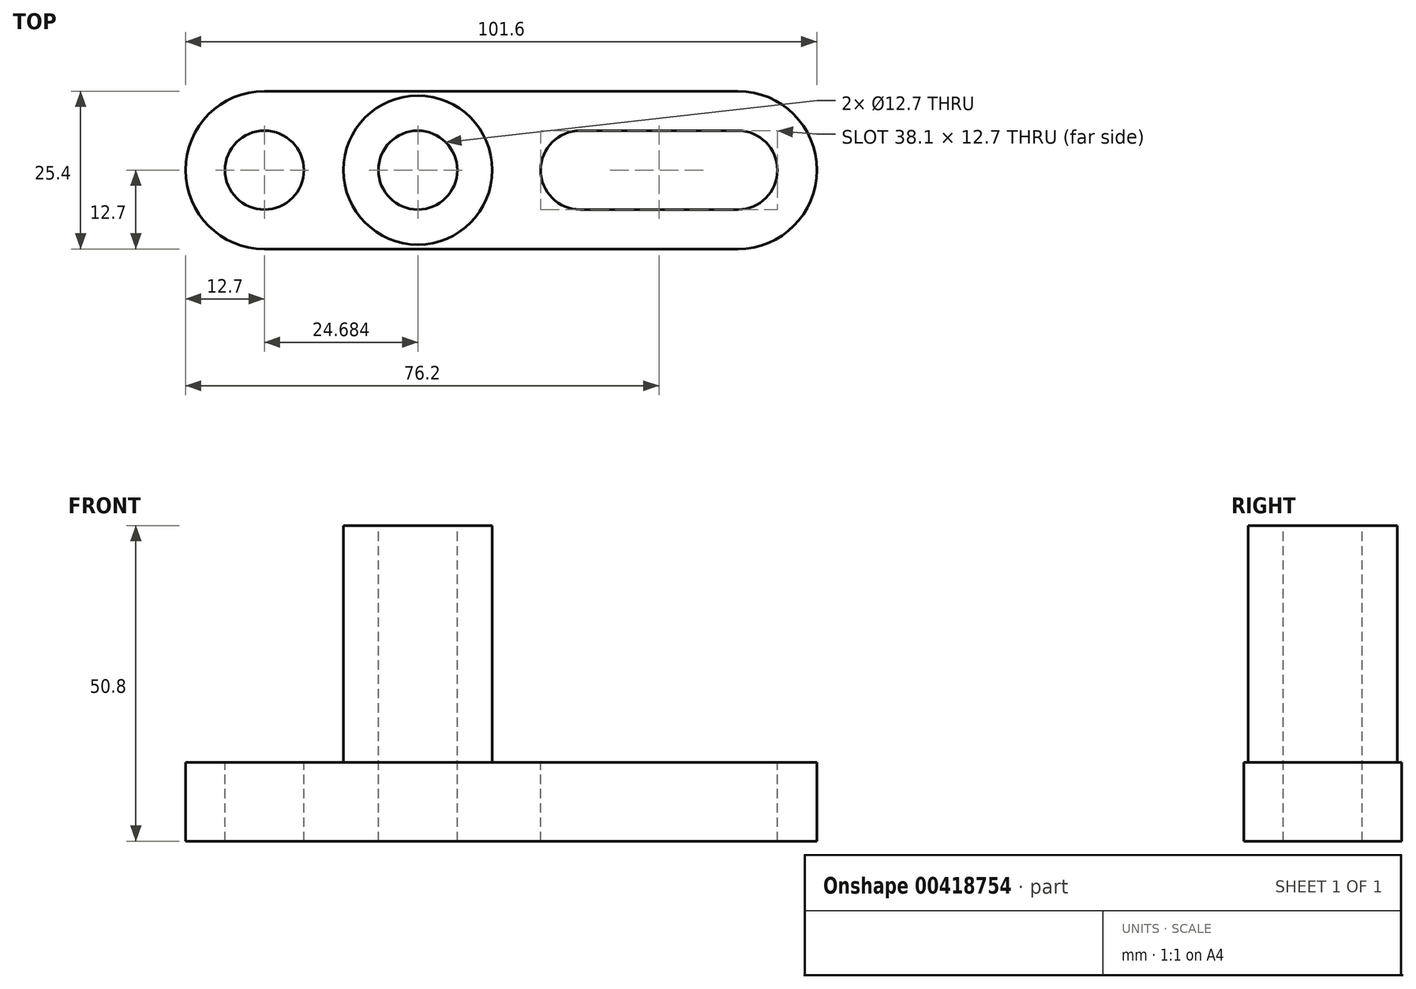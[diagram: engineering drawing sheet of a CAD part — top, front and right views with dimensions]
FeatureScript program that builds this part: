
annotation { "Feature Type Name" : "Feature", "Feature Type Description" : "" }
export const myFeature = defineFeature(function(context is Context, id is Id, definition is map)
    precondition{}
    {
        {
            var Q0;
            Q0=qCreatedBy(makeId("Front.planeOp"),FACE);
            var sketch = newSketch(context, id + "F0", { "sketchPlane" : qUnion([Q0])});
            skLineSegment(sketch, "E0", {"start": v(0, 0) * mm, "end": v(101.6, 0) * mm});
            skLineSegment(sketch, "E1", {"start": v(101.6, 0) * mm, "end": v(101.6, 12.7) * mm});
            skLineSegment(sketch, "E2", {"start": v(101.6, 12.7) * mm, "end": v(0, 12.7) * mm});
            skLineSegment(sketch, "E3", {"start": v(0, 12.7) * mm, "end": v(0, 0) * mm});
            skSolve(sketch);
        }
        {
            var Q0;
            Q0 = qSketchRegion(id + "F0", true);
            extrude(context, id + "F1", {"entities" : qUnion([Q0]), "depth" : 25.4 * mm});
        }
        {
            var Q0;
            {var subQ0=sQuery(id+"F0.wireOp",EDGE,"E2");var subQ1=makeQuery(id+"F1.opExtrude","SWEPT_FACE",FACE,{"disambiguationData":[OSD([subQ0])]});var subQ2=sQuery(id+"F0.wireOp",EDGE,"E1");Q0=makeQuery(id+"FwOSXB9rs8ltbqY_1.boolean.opBoolean","SPLIT",FACE,{"disambiguationData":[TD([makeQuery(id+"F1.opExtrude","SWEPT_FACE",FACE,{"disambiguationData":[OSD([subQ2])]})])],"derivedFrom":subQ1});}
            var sketch = newSketch(context, id + "F2", { "sketchPlane" : qUnion([Q0])});
            skArc(sketch, "E4", {"start": v(88.9, -25.4) * mm, "mid": v(101.6, -12.7) * mm, "end": v(88.9, 0) * mm});
            skArc(sketch, "E5", {"start": v(12.7, 0) * mm, "mid": v(0, -13.14) * mm, "end": v(12.67, -26.32) * mm});
            skSolve(sketch);
        }
        {
            var Q0;
            {var subQ0=sQuery(id+"F2.wireOp",EDGE,"E4");var subQ1=sQuery(id+"F0.wireOp",EDGE,"E2");var subQ2=sQuery(id+"F0.wireOp",EDGE,"E1");var subQ5=makeQuery(id+"F1.opExtrude","SWEPT_EDGE",EDGE,{"disambiguationData":[OSD([subQ2,subQ1])]});var subQ6=makeQuery(id+"F2.imprint","INTERSECT",VERTEX,{"derivedFrom":[subQ5,subQ0]});Q0=makeQuery(id+"F2.imprint","IMPRINT",FACE,{"disambiguationData":[TD([[makeQuery(id+"F2.imprint","IMPRINT",EDGE,{"disambiguationData":[TD([[subQ6,-1.0]])],"derivedFrom":subQ0}),-1.0]])]});}
            var Q1;
            {var subQ0=sQuery(id+"F2.wireOp",EDGE,"E4");var subQ1=sQuery(id+"F0.wireOp",EDGE,"E2");var subQ2=sQuery(id+"F0.wireOp",EDGE,"E1");var subQ5=makeQuery(id+"F1.opExtrude","SWEPT_EDGE",EDGE,{"disambiguationData":[OSD([subQ2,subQ1])]});var subQ6=makeQuery(id+"F2.imprint","INTERSECT",VERTEX,{"derivedFrom":[subQ5,subQ0]});Q1=makeQuery(id+"F2.imprint","IMPRINT",FACE,{"disambiguationData":[TD([[makeQuery(id+"F2.imprint","IMPRINT",EDGE,{"disambiguationData":[TD([[subQ6,1.0]])],"derivedFrom":subQ0}),-1.0]])]});}
            extrude(context, id + "F3", {"entities" : qUnion([Q0, Q1]), "operationType" : NewBodyOperationType.REMOVE, "oppositeDirection" : true, "depth" : 25.4 * mm});
        }
        {
            var Q0;
            {var subQ0=sQuery(id+"F0.wireOp",EDGE,"E3");var subQ1=sQuery(id+"F0.wireOp",EDGE,"E2");var subQ2=makeQuery(id+"F1.opExtrude","SWEPT_FACE",FACE,{"disambiguationData":[OSD([subQ1])]});Q0=makeQuery(id+"FwOSXB9rs8ltbqY_1.boolean.opBoolean","SPLIT",FACE,{"disambiguationData":[TD([makeQuery(id+"F1.opExtrude","SWEPT_FACE",FACE,{"disambiguationData":[OSD([subQ0])]})])],"derivedFrom":subQ2});}
            var sketch = newSketch(context, id + "F4", { "sketchPlane" : qUnion([Q0])});
            skArc(sketch, "E6", {"start": v(12.7, 0) * mm, "mid": v(0, -12.7) * mm, "end": v(12.7, -25.4) * mm});
            skSolve(sketch);
        }
        {
            var Q0;
            {var subQ0=sQuery(id+"F4.wireOp",EDGE,"E6");var subQ1=sQuery(id+"F0.wireOp",EDGE,"E3");var subQ2=sQuery(id+"F0.wireOp",EDGE,"E2");var subQ5=makeQuery(id+"F1.opExtrude","SWEPT_EDGE",EDGE,{"disambiguationData":[OSD([subQ2,subQ1])]});var subQ6=makeQuery(id+"F4.imprint","INTERSECT",VERTEX,{"derivedFrom":[subQ5,subQ0]});Q0=makeQuery(id+"F4.imprint","IMPRINT",FACE,{"disambiguationData":[TD([[makeQuery(id+"F4.imprint","IMPRINT",EDGE,{"disambiguationData":[TD([[subQ6,1.0]])],"derivedFrom":subQ0}),-1.0]])]});}
            var Q1;
            {var subQ0=sQuery(id+"F4.wireOp",EDGE,"E6");var subQ1=sQuery(id+"F0.wireOp",EDGE,"E3");var subQ2=sQuery(id+"F0.wireOp",EDGE,"E2");var subQ5=makeQuery(id+"F1.opExtrude","SWEPT_EDGE",EDGE,{"disambiguationData":[OSD([subQ2,subQ1])]});var subQ6=makeQuery(id+"F4.imprint","INTERSECT",VERTEX,{"derivedFrom":[subQ5,subQ0]});Q1=makeQuery(id+"F4.imprint","IMPRINT",FACE,{"disambiguationData":[TD([[makeQuery(id+"F4.imprint","IMPRINT",EDGE,{"disambiguationData":[TD([[subQ6,-1.0]])],"derivedFrom":subQ0}),-1.0]])]});}
            extrude(context, id + "F5", {"entities" : qUnion([Q0, Q1]), "operationType" : NewBodyOperationType.REMOVE, "oppositeDirection" : true, "depth" : 25.4 * mm});
        }
        {
            var Q0;
            Q0=makeQuery(id+"F1.opExtrude","SWEPT_FACE",FACE,{"disambiguationData":[OSD([sQuery(id+"F0.wireOp",EDGE,"E2")])]});
            var sketch = newSketch(context, id + "F6", { "sketchPlane" : qUnion([Q0])});
            skCircle(sketch, "E7", {"center": v(12.7, -12.7) * mm, "radius": 6.35 * mm});
            skSolve(sketch);
        }
        {
            var Q0;
            Q0 = qSketchRegion(id + "F6", true);
            extrude(context, id + "F7", {"entities" : qUnion([Q0]), "operationType" : NewBodyOperationType.REMOVE, "oppositeDirection" : true, "depth" : 25.4 * mm});
        }
        {
            var Q0;
            Q0=makeQuery(id+"F1.opExtrude","SWEPT_FACE",FACE,{"disambiguationData":[OSD([sQuery(id+"F0.wireOp",EDGE,"E2")])]});
            var sketch = newSketch(context, id + "F8", { "sketchPlane" : qUnion([Q0])});
            skCircle(sketch, "E8", {"center": v(37.38, -12.7) * mm, "radius": 11.98 * mm});
            skSolve(sketch);
        }
        {
            var Q0;
            Q0=makeQuery(id+"F8.imprint","IMPRINT",FACE,{"disambiguationData":[TD([[makeQuery(id+"F8.imprint","IMPRINT",EDGE,{"derivedFrom":sQuery(id+"F8.wireOp",EDGE,"E8")}),1.0]])]});
            extrude(context, id + "F9", {"entities" : qUnion([Q0]), "operationType" : NewBodyOperationType.ADD, "depth" : 38.1 * mm});
        }
        {
            var Q0;
            Q0=makeQuery(id+"F9.opExtrude","CAP_FACE",FACE,{"disambiguationData":[OSD([sQuery(id+"F8.wireOp",EDGE,"E8")])],"isStart":false});
            var sketch = newSketch(context, id + "F10", { "sketchPlane" : qUnion([Q0])});
            skCircle(sketch, "E9", {"center": v(37.38, -12.7) * mm, "radius": 6.35 * mm});
            skSolve(sketch);
        }
        {
            var Q0;
            Q0=makeQuery(id+"F10.imprint","IMPRINT",FACE,{"disambiguationData":[TD([[makeQuery(id+"F10.imprint","IMPRINT",EDGE,{"derivedFrom":sQuery(id+"F10.wireOp",EDGE,"E9")}),1.0]])]});
            extrude(context, id + "F11", {"entities" : qUnion([Q0]), "operationType" : NewBodyOperationType.REMOVE, "oppositeDirection" : true, "depth" : 50.8 * mm});
        }
        {
            var Q0;
            Q0=makeQuery(id+"F1.opExtrude","SWEPT_FACE",FACE,{"disambiguationData":[OSD([sQuery(id+"F0.wireOp",EDGE,"E2")])]});
            var sketch = newSketch(context, id + "F12", { "sketchPlane" : qUnion([Q0])});
            skCircle(sketch, "E10", {"center": v(63.5, -12.7) * mm, "radius": 6.35 * mm});
            skCircle(sketch, "E11", {"center": v(88.9, -12.7) * mm, "radius": 6.35 * mm});
            skLineSegment(sketch, "E12", {"start": v(63.5, -19.05) * mm, "end": v(88.9, -19.05) * mm});
            skLineSegment(sketch, "E13", {"start": v(63.5, -6.35) * mm, "end": v(88.9, -6.35) * mm});
            skSolve(sketch);
        }
        {
            var Q0;
            {var subQ0=sQuery(id+"F12.wireOp",EDGE,"E10");var subQ1=makeQuery(id+"F12.imprint","INTERSECT",VERTEX,{"derivedFrom":[subQ0,sQuery(id+"F12.wireOp",EDGE,"E12")]});Q0=makeQuery(id+"F12.imprint","IMPRINT",FACE,{"disambiguationData":[TD([[makeQuery(id+"F12.imprint","IMPRINT",EDGE,{"disambiguationData":[TD([[subQ1,1.0]])],"derivedFrom":subQ0}),1.0]])]});}
            var Q1;
            {var subQ0=sQuery(id+"F12.wireOp",EDGE,"E12");Q1=makeQuery(id+"F12.imprint","IMPRINT",FACE,{"disambiguationData":[TD([[makeQuery(id+"F12.imprint","IMPRINT",EDGE,{"derivedFrom":subQ0}),1.0]])]});}
            var Q2;
            {var subQ0=sQuery(id+"F12.wireOp",EDGE,"E11");var subQ1=makeQuery(id+"F12.imprint","INTERSECT",VERTEX,{"derivedFrom":[subQ0,sQuery(id+"F12.wireOp",EDGE,"E12")]});Q2=makeQuery(id+"F12.imprint","IMPRINT",FACE,{"disambiguationData":[TD([[makeQuery(id+"F12.imprint","IMPRINT",EDGE,{"disambiguationData":[TD([[subQ1,1.0]])],"derivedFrom":subQ0}),1.0]])]});}
            extrude(context, id + "F13", {"entities" : qUnion([Q0, Q1, Q2]), "operationType" : NewBodyOperationType.REMOVE, "oppositeDirection" : true, "depth" : 12.7 * mm});
        }
    });
